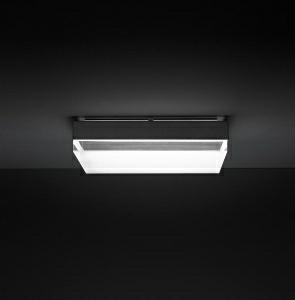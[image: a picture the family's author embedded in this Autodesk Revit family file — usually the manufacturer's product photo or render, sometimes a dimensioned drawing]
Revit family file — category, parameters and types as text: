
# Revit family: spectral_perga_perga-qa_422_2600-840_ws_0be9
name_source: partatom
category: Lighting Fixtures
revit_build: Autodesk Revit 2016 (Build: 20150220_1215(x64)
units: mm (PartAtom-declared; Revit-internal decimal feet)

## family parameters
Cut with Voids When Loaded = No
Host = Face
Light Source = No
Part Type = Normal
Room Calculation Point = No
Round Connector Dimension = Use Diameter
Shared = No

## types (1)
- SPECTRAL PERGA (1 x )
    Apparent Load = 0 VA
    Approval mark = CE
    CIE Flux Codes = 46 78 95 88 63
    Control Gear = Electronic transformer
    Default Elevation = 1800 mm
    Description = SPP0000011
PERGAMENT surface mounted

Design:
Square luminaire element comprising an acrylic glass block with transparent superpolished exterior. Underneath painted matt to reduce glare. Luminaire
element integrated in an outer steel powder-coated sectional aluminium square frame. The acrylic block is scratchproof and insensitive to fingerprints, and is connected to a poweder-coated metal body by a bayonet and snap fastening. The metal body accommodates the electrical components and electronic ballast. The LED module is formed as a square LED flat board and can be removed for installation or exchange using a fold-out LED carrier. Plug-in electrical connection of the LED flat board. Luminaire with heat-resistant wiring. Homogenous illumination of the light surface. Suitable for ceiling or wall mounting. Light colours 830 or 840. Also in a dimmable version.
Protection rating IP20, safety class I.

Colour:
Metal body – similar to RAL 9016 white silk matt
Frame – white (WS), silver (SI), black (AQ)
    Height = 98 mm
    Lamp = 1 x
    Lamp count = 1
    Length = 422 mm
    Luminous efficacy = 0 lm/W
    Manufacturer = Ridi
    ModVariant = No
    Model = PERGA-QA 422/2600-840 WS
    Mounting Place = Ceiling
    Mounting Type = Surface mounted
    Number of Poles = 1
    OnlyDefault = Yes
    Power Factor = 1
    Product Name = SPECTRAL PERGA
    Product group = Ceiling mounted luminaire
    ProductGroupID = 3
    Protection Class = Protection class
    Protection Degree = IP 20
    RlxData = <blob elided: 30989 chars, md5=b365a436>
    Socket = socket
    Standby Power = 0 W
    System Light Flux = 0 lm
    System Power = 0 W
    Type Image = pergament005b.jpg
    URL = http://reluxnet.relux.com
    VarID = 1
    Voltage = 0 V
    Weight = 0.00 kg
    Width = 422 mm

## geometry (parser evidence)
native form markers: Blend x4, Sweep x11
no freeform markers — native parametric forms only
